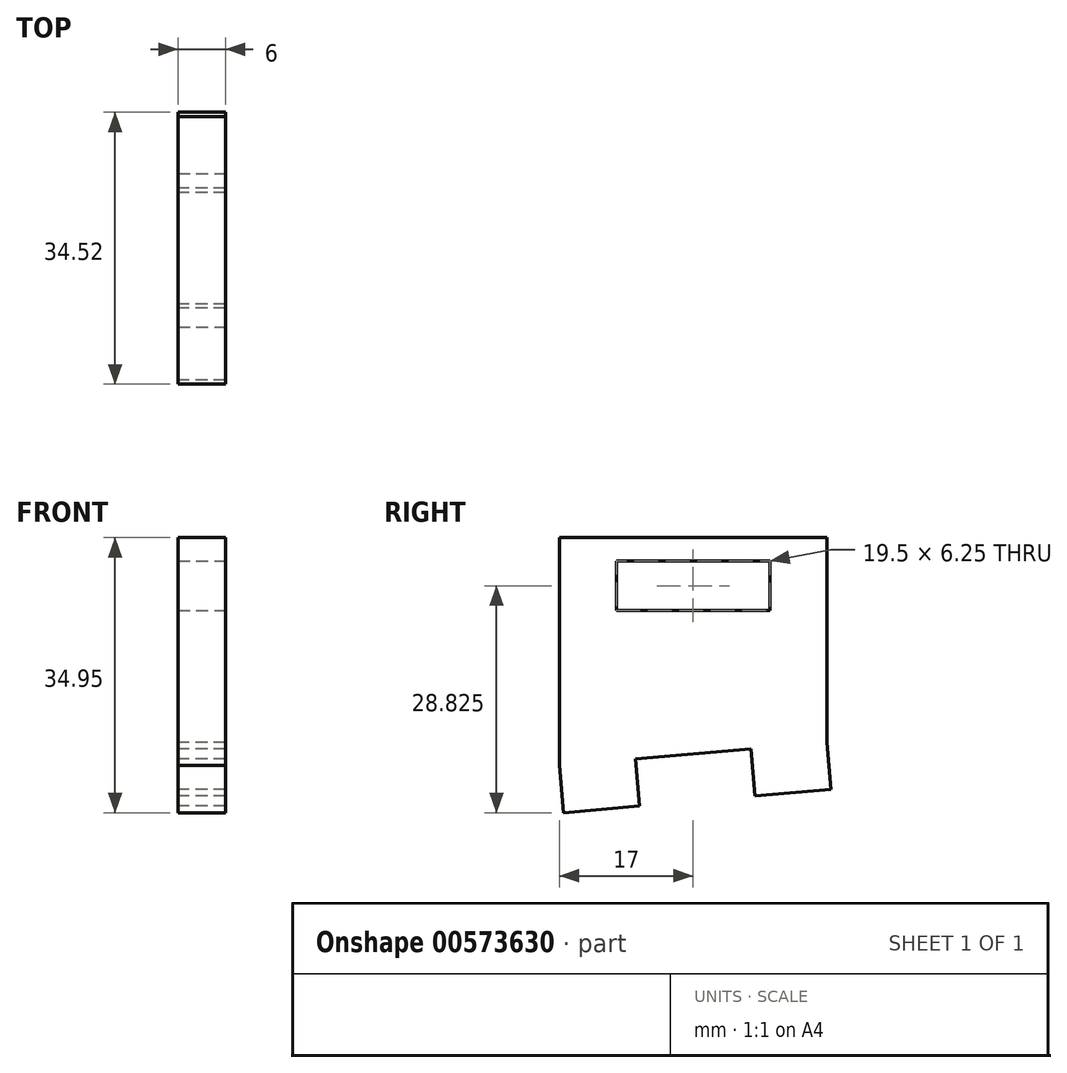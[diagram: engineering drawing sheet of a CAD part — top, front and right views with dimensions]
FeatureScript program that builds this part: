
annotation { "Feature Type Name" : "Feature", "Feature Type Description" : "" }
export const myFeature = defineFeature(function(context is Context, id is Id, definition is map)
    precondition{}
    {
        {
            var Q0;
            Q0=qCreatedBy(makeId("Right.planeOp"),FACE);
            var sketch = newSketch(context, id + "F0", { "sketchPlane" : qUnion([Q0])});
            skLineSegment(sketch, "E0.top", {"start": v(17, 0) * mm, "end": v(-17, 0) * mm});
            skLineSegment(sketch, "E0.left", {"start": v(17, -26) * mm, "end": v(17, 0) * mm});
            skLineSegment(sketch, "E0.right", {"start": v(-17, -28.97) * mm, "end": v(-17, 0) * mm});
            skPoint(sketch, "E0.middle", {"position": v(0, 0) * mm});
            skLineSegment(sketch, "E1", {"start": v(-17, -28.97) * mm, "end": v(17, -26) * mm});
            skLineSegment(sketch, "E2", {"start": v(17, -26) * mm, "end": v(-17, -26) * mm, "construction": true});
            skSolve(sketch);
        }
        {
            var Q0;
            Q0 = qSketchRegion(id + "F0", true);
            extrude(context, id + "F1", {"entities" : qUnion([Q0]), "endBound" : BoundingType.SYMMETRIC, "depth" : 6 * mm, "offsetDistance" : 25 * mm});
        }
        {
            var Q0;
            Q0=qCreatedBy(makeId("Right.planeOp"),FACE);
            var sketch = newSketch(context, id + "F2", { "sketchPlane" : qUnion([Q0])});
            skLineSegment(sketch, "E3", {"start": v(-16.48, -34.95) * mm, "end": v(-6.82, -34.1) * mm});
            skLineSegment(sketch, "E4", {"start": v(-6.82, -34.1) * mm, "end": v(-7.35, -28.13) * mm});
            skLineSegment(sketch, "E5", {"start": v(-7.35, -28.13) * mm, "end": v(-17, -28.97) * mm});
            skLineSegment(sketch, "E6", {"start": v(-17, -28.97) * mm, "end": v(-16.48, -34.95) * mm});
            skLineSegment(sketch, "E7", {"start": v(0, -27.49) * mm, "end": v(0.68, -35.3) * mm, "construction": true});
            skLineSegment(sketch, "E8.MirrorCS", {"start": v(17, -26) * mm, "end": v(17.52, -31.98) * mm});
            skLineSegment(sketch, "E9.MirrorCS", {"start": v(7.35, -26.84) * mm, "end": v(17, -26) * mm});
            skLineSegment(sketch, "E10.MirrorCS", {"start": v(7.87, -32.82) * mm, "end": v(7.35, -26.84) * mm});
            skLineSegment(sketch, "E11.MirrorCS", {"start": v(17.52, -31.98) * mm, "end": v(7.87, -32.82) * mm});
            skSolve(sketch);
        }
        {
            var Q0;
            Q0 = qSketchRegion(id + "F2", true);
            extrude(context, id + "F3", {"entities" : qUnion([Q0]), "operationType" : NewBodyOperationType.ADD, "endBound" : BoundingType.SYMMETRIC, "depth" : 6 * mm, "offsetDistance" : 25 * mm});
        }
        {
            var Q0;
            {var subQ0=sQuery(id+"F0.wireOp",EDGE,"E1");var subQ1=sQuery(id+"F0.wireOp",EDGE,"E0.right");var subQ2=sQuery(id+"F0.wireOp",EDGE,"E0.left");var subQ3=sQuery(id+"F0.wireOp",EDGE,"E0.top");Q0=makeQuery(id+"FRKY4pzqr8ala3Q_1.boolean.opBoolean","MERGE",FACE,{"derivedFrom":[makeQuery(id+"F1.opExtrude","CAP_FACE",FACE,{"disambiguationData":[OSD([subQ3,subQ2,subQ1,subQ0])],"isStart":false}),makeQuery(id+"FRKY4pzqr8ala3Q_1.opExtrude","CAP_FACE",FACE,{"disambiguationData":[OSD([subQ3,subQ2,subQ1,subQ0]),OD(0.0)],"isStart":false}),makeQuery(id+"FRKY4pzqr8ala3Q_1.opExtrude","CAP_FACE",FACE,{"disambiguationData":[OSD([subQ3,subQ2,subQ1,subQ0]),OD(1.0)],"isStart":false})]});}
            var sketch = newSketch(context, id + "F4", { "sketchPlane" : qUnion([Q0])});
            skLineSegment(sketch, "E12.bottom", {"start": v(9.75, -9.25) * mm, "end": v(-9.75, -9.25) * mm});
            skLineSegment(sketch, "E12.top", {"start": v(9.75, -3) * mm, "end": v(-9.75, -3) * mm});
            skLineSegment(sketch, "E12.left", {"start": v(9.75, -9.25) * mm, "end": v(9.75, -3) * mm});
            skLineSegment(sketch, "E12.right", {"start": v(-9.75, -9.25) * mm, "end": v(-9.75, -3) * mm});
            skPoint(sketch, "E12.middle", {"position": v(0, -6.12) * mm});
            skSolve(sketch);
        }
        {
            var Q0;
            Q0=makeQuery(id+"F4.imprint","IMPRINT",FACE,{"disambiguationData":[TD([[makeQuery(id+"F4.imprint","IMPRINT",EDGE,{"derivedFrom":sQuery(id+"F4.wireOp",EDGE,"E12.bottom")}),-1.0]])]});
            var Q1;
            Q1=makeQuery(id+"F1.opExtrude","CAP_FACE",FACE,{"disambiguationData":[OSD([sQuery(id+"F0.wireOp",EDGE,"E0.top"),sQuery(id+"F0.wireOp",EDGE,"E0.left"),sQuery(id+"F0.wireOp",EDGE,"E0.right"),sQuery(id+"F0.wireOp",EDGE,"E1")])],"isStart":true});
            extrude(context, id + "F5", {"entities" : qUnion([Q0]), "operationType" : NewBodyOperationType.REMOVE, "endBound" : BoundingType.UP_TO_NEXT, "oppositeDirection" : true, "depth" : 6 * mm, "endBoundEntityFace" : qUnion([Q1]), "offsetDistance" : 25 * mm});
        }
    });
